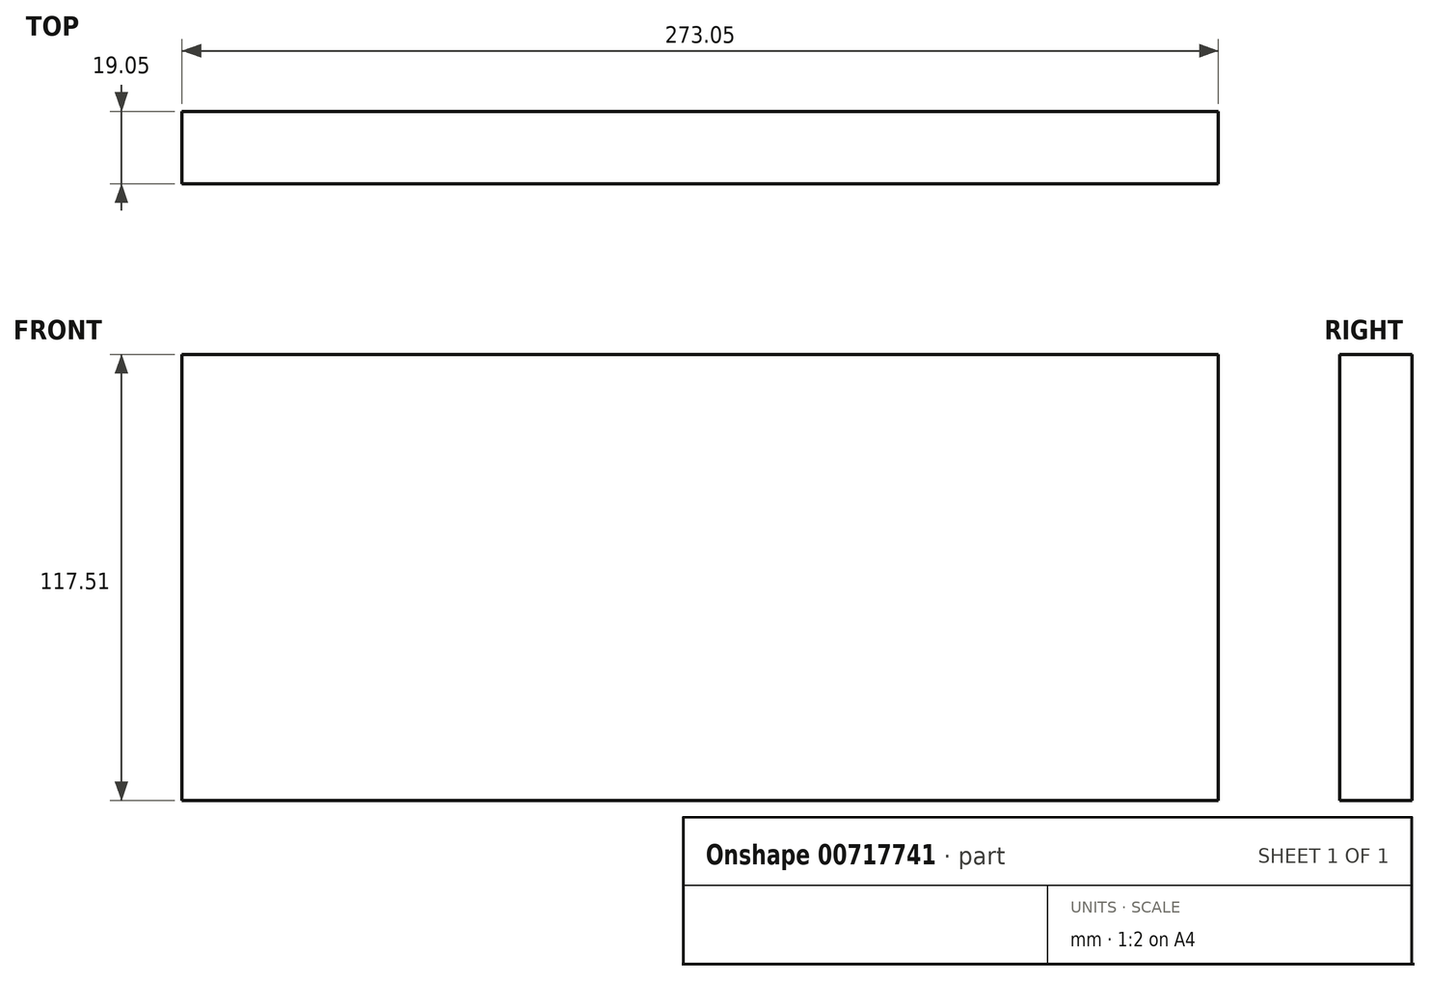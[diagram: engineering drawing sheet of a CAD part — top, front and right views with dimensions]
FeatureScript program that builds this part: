
annotation { "Feature Type Name" : "Feature", "Feature Type Description" : "" }
export const myFeature = defineFeature(function(context is Context, id is Id, definition is map)
    precondition{}
    {
        {
            var Q0;
            Q0=qCreatedBy(makeId("Front.planeOp"),FACE);
            var sketch = newSketch(context, id + "F0", { "sketchPlane" : qUnion([Q0])});
            skLineSegment(sketch, "E0.bottom", {"start": v(-87.36, 113.62) * mm, "end": v(185.7, 113.62) * mm});
            skLineSegment(sketch, "E0.top", {"start": v(-87.36, -3.9) * mm, "end": v(185.7, -3.9) * mm});
            skLineSegment(sketch, "E0.left", {"start": v(-87.36, 113.62) * mm, "end": v(-87.36, -3.9) * mm});
            skLineSegment(sketch, "E0.right", {"start": v(185.7, 113.62) * mm, "end": v(185.7, -3.9) * mm});
            skSolve(sketch);
        }
        {
            var Q0;
            Q0=makeQuery(id+"F0.imprint","IMPRINT",FACE,{"disambiguationData":[TD([[makeQuery(id+"F0.imprint","IMPRINT",EDGE,{"derivedFrom":sQuery(id+"F0.wireOp",EDGE,"E0.bottom")}),-1.0]])]});
            extrude(context, id + "F1", {"entities" : qUnion([Q0]), "depth" : 19.05 * mm, "offsetDistance" : 25.4 * mm});
        }
    });
